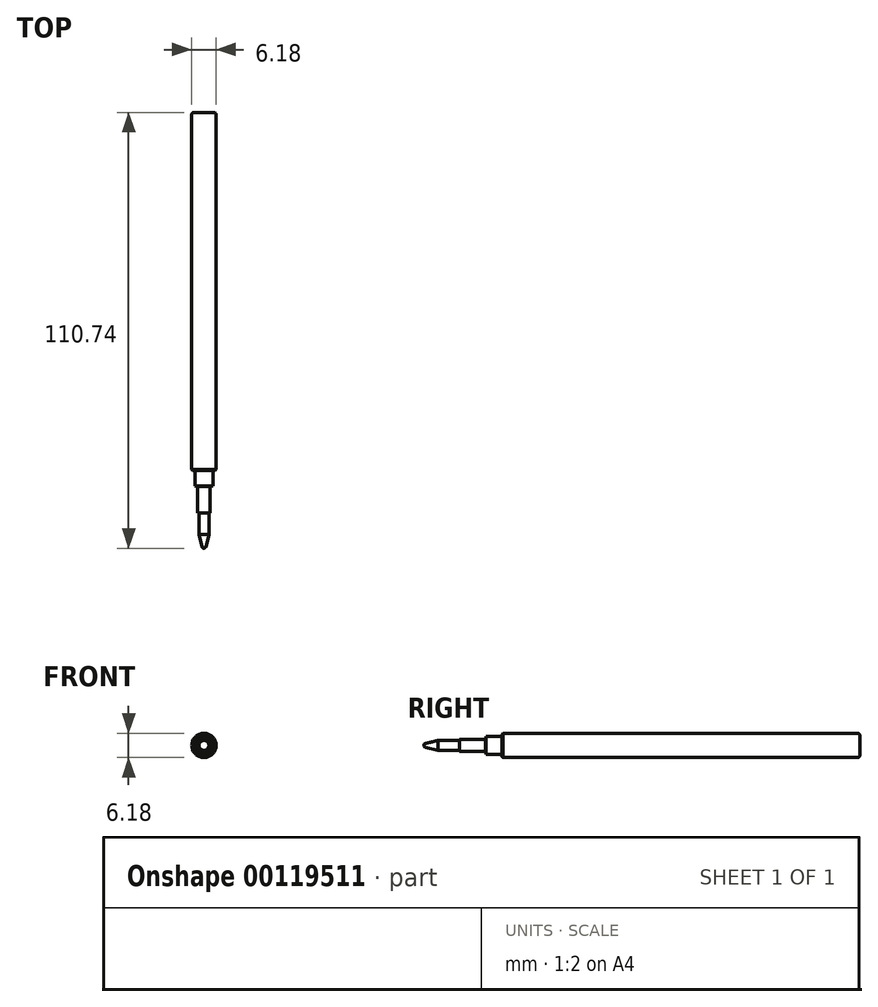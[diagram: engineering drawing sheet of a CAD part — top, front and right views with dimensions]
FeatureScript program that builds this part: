
annotation { "Feature Type Name" : "Feature", "Feature Type Description" : "" }
export const myFeature = defineFeature(function(context is Context, id is Id, definition is map)
    precondition{}
    {
        {
            var Q0;
            Q0=qCreatedBy(makeId("Right.planeOp"),FACE);
            var sketch = newSketch(context, id + "F0", { "sketchPlane" : qUnion([Q0])});
            skLineSegment(sketch, "E0.bottom", {"start": v(-50.8, 0) * mm, "end": v(40.13, 0) * mm});
            skLineSegment(sketch, "E0.top", {"start": v(-50.8, 3.09) * mm, "end": v(40.13, 3.09) * mm});
            skLineSegment(sketch, "E0.left", {"start": v(-50.8, 0) * mm, "end": v(-50.8, 3.09) * mm});
            skLineSegment(sketch, "E0.right", {"start": v(40.13, 0) * mm, "end": v(40.13, 3.09) * mm});
            skSolve(sketch);
        }
        {
            var Q0;
            Q0=makeQuery(id+"F0.imprint","IMPRINT",FACE,{"disambiguationData":[TD([[makeQuery(id+"F0.imprint","IMPRINT",EDGE,{"derivedFrom":sQuery(id+"F0.wireOp",EDGE,"E0.bottom")}),1.0]])]});
            var Q1;
            Q1=sQuery(id+"F0.wireOp",EDGE,"E0.bottom");
            revolve(context, id + "F1", {"entities" : qUnion([Q0]), "axis" : qUnion([Q1]), "revolveType" : RevolveType.FULL});
        }
        {
            var Q0;
            Q0=qCreatedBy(makeId("Right.planeOp"),FACE);
            var sketch = newSketch(context, id + "F2", { "sketchPlane" : qUnion([Q0])});
            skLineSegment(sketch, "E1", {"start": v(-50.8, 0) * mm, "end": v(-70.61, 0) * mm});
            skLineSegment(sketch, "E2", {"start": v(-50.8, 0) * mm, "end": v(-50.8, 1.24) * mm});
            skArc(sketch, "E3", {"start": v(-70.22, 0.5) * mm, "mid": v(-70.5, 0.32) * mm, "end": v(-70.61, 0) * mm});
            skLineSegment(sketch, "E4", {"start": v(-67.06, 1.24) * mm, "end": v(-70.22, 0.5) * mm});
            skLineSegment(sketch, "E5", {"start": v(-50.8, 1.24) * mm, "end": v(-50.8, 2.29) * mm});
            skLineSegment(sketch, "E6", {"start": v(-50.8, 2.29) * mm, "end": v(-54.76, 2.29) * mm});
            skLineSegment(sketch, "E7", {"start": v(-54.76, 2.29) * mm, "end": v(-54.97, 1.57) * mm});
            skLineSegment(sketch, "E8", {"start": v(-61.6, 1.24) * mm, "end": v(-61.6, 1.57) * mm});
            skLineSegment(sketch, "E9", {"start": v(-61.6, 1.57) * mm, "end": v(-54.97, 1.57) * mm});
            skLineSegment(sketch, "E10.trimOffspring", {"start": v(-61.6, 1.24) * mm, "end": v(-67.06, 1.24) * mm});
            skPoint(sketch, "E11.orphan", {"position": v(-55.07, 1.24) * mm});
            skSolve(sketch);
        }
        {
            var Q0;
            Q0 = qSketchRegion(id + "F2", true);
            var Q1;
            Q1=sQuery(id+"F2.wireOp",EDGE,"E1");
            revolve(context, id + "F3", {"operationType" : NewBodyOperationType.ADD, "entities" : qUnion([Q0]), "axis" : qUnion([Q1]), "revolveType" : RevolveType.FULL});
        }
        {
            var Q0;
            Q0=makeQuery(id+"F1.opRevolve","SWEPT_EDGE",EDGE,{"disambiguationData":[OSD([sQuery(id+"F0.wireOp",EDGE,"E0.top"),sQuery(id+"F0.wireOp",EDGE,"E0.left")])]});
            chamfer(context, id + "F4", {"entities" : qUnion([Q0]), "width" : 0.25 * mm, "tangentPropagation" : true});
        }
        {
            var Q0;
            Q0=makeQuery(id+"F1.opRevolve","SWEPT_EDGE",EDGE,{"disambiguationData":[OSD([sQuery(id+"F0.wireOp",EDGE,"E0.top"),sQuery(id+"F0.wireOp",EDGE,"E0.right")])]});
            fillet(context, id + "F5", {"entities" : qUnion([Q0]), "radius" : 0.5 * mm, "tangentPropagation" : true, "allowEdgeOverflow" : false});
        }
    });
